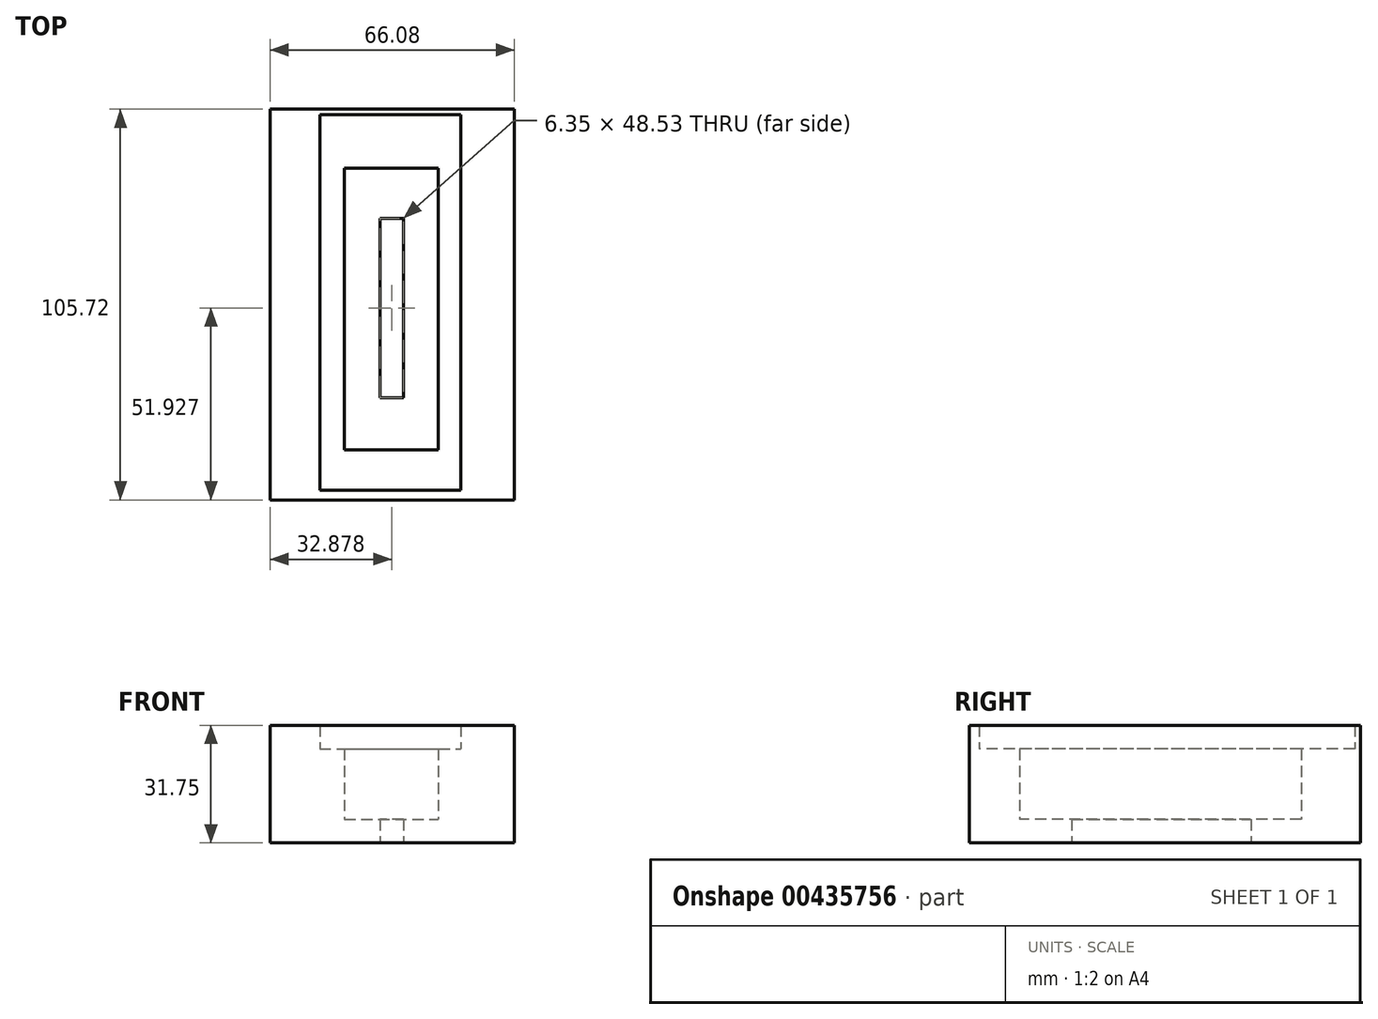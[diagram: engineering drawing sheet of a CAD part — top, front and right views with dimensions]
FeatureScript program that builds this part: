
annotation { "Feature Type Name" : "Feature", "Feature Type Description" : "" }
export const myFeature = defineFeature(function(context is Context, id is Id, definition is map)
    precondition{}
    {
        {
            var Q0;
            Q0=qCreatedBy(makeId("Top.planeOp"),FACE);
            var sketch = newSketch(context, id + "F0", { "sketchPlane" : qUnion([Q0])});
            skLineSegment(sketch, "E0.bottom", {"start": v(-32.9, 52.86) * mm, "end": v(33.19, 52.86) * mm});
            skLineSegment(sketch, "E0.top", {"start": v(-32.9, -52.86) * mm, "end": v(33.19, -52.86) * mm});
            skLineSegment(sketch, "E0.left", {"start": v(-32.9, 52.86) * mm, "end": v(-32.9, -52.86) * mm});
            skLineSegment(sketch, "E0.right", {"start": v(33.19, 52.86) * mm, "end": v(33.19, -52.86) * mm});
            skSolve(sketch);
        }
        {
            var Q0;
            Q0 = qSketchRegion(id + "F0", true);
            var Q1;
            Q1=makeQuery(id+"F0.imprint","IMPRINT",FACE,{"disambiguationData":[TD([[makeQuery(id+"F0.imprint","IMPRINT",EDGE,{"derivedFrom":sQuery(id+"F0.wireOp",EDGE,"E0.bottom")}),-1.0]])]});
            extrude(context, id + "F1", {"entities" : qUnion([Q0, Q1]), "depth" : 6.35 * mm});
        }
        {
            var Q0;
            Q0=makeQuery(id+"F1.opExtrude","CAP_FACE",FACE,{"disambiguationData":[OSD([sQuery(id+"F0.wireOp",EDGE,"E0.bottom"),sQuery(id+"F0.wireOp",EDGE,"E0.top"),sQuery(id+"F0.wireOp",EDGE,"E0.left"),sQuery(id+"F0.wireOp",EDGE,"E0.right")])],"isStart":false});
            var sketch = newSketch(context, id + "F2", { "sketchPlane" : qUnion([Q0])});
            skLineSegment(sketch, "E1.bottom", {"start": v(-19.5, 51.39) * mm, "end": v(18.6, 51.39) * mm});
            skLineSegment(sketch, "E1.top", {"start": v(-19.5, -50.21) * mm, "end": v(18.6, -50.21) * mm});
            skLineSegment(sketch, "E1.left", {"start": v(-19.5, 51.39) * mm, "end": v(-19.5, -50.21) * mm});
            skLineSegment(sketch, "E1.right", {"start": v(18.6, 51.39) * mm, "end": v(18.6, -50.21) * mm});
            skLineSegment(sketch, "E2.bottom", {"start": v(-10.32, 39.4) * mm, "end": v(10.5, 39.4) * mm});
            skLineSegment(sketch, "E2.top", {"start": v(-10.32, -41.4) * mm, "end": v(10.5, -41.4) * mm});
            skLineSegment(sketch, "E2.left", {"start": v(-10.32, 39.4) * mm, "end": v(-10.32, -41.4) * mm});
            skLineSegment(sketch, "E2.right", {"start": v(10.5, 39.4) * mm, "end": v(10.5, -41.4) * mm});
            skLineSegment(sketch, "E3.bottom", {"start": v(-3.62, 27.05) * mm, "end": v(3.44, 27.05) * mm});
            skLineSegment(sketch, "E3.top", {"start": v(-3.62, -32.57) * mm, "end": v(3.44, -32.57) * mm});
            skLineSegment(sketch, "E3.left", {"start": v(-3.62, 27.05) * mm, "end": v(-3.62, -32.57) * mm});
            skLineSegment(sketch, "E3.right", {"start": v(3.44, 27.05) * mm, "end": v(3.44, -32.57) * mm});
            skSolve(sketch);
        }
        {
            var Q0;
            Q0=makeQuery(id+"F2.imprint","IMPRINT",FACE,{"disambiguationData":[TD([[makeQuery(id+"F2.imprint","IMPRINT",EDGE,{"derivedFrom":sQuery(id+"F2.wireOp",EDGE,"E1.bottom")}),1.0]])]});
            extrude(context, id + "F3", {"entities" : qUnion([Q0]), "operationType" : NewBodyOperationType.ADD, "depth" : 25.4 * mm});
        }
        {
            var Q0;
            Q0=makeQuery(id+"F1.opExtrude","CAP_FACE",FACE,{"disambiguationData":[OSD([sQuery(id+"F0.wireOp",EDGE,"E0.bottom"),sQuery(id+"F0.wireOp",EDGE,"E0.top"),sQuery(id+"F0.wireOp",EDGE,"E0.left"),sQuery(id+"F0.wireOp",EDGE,"E0.right")])],"isStart":false});
            var sketch = newSketch(context, id + "F4", { "sketchPlane" : qUnion([Q0])});
            skLineSegment(sketch, "E4.bottom", {"start": v(-12.83, 36.9) * mm, "end": v(12.57, 36.9) * mm});
            skLineSegment(sketch, "E4.top", {"start": v(-12.83, -39.3) * mm, "end": v(12.57, -39.3) * mm});
            skLineSegment(sketch, "E4.left", {"start": v(-12.83, 36.9) * mm, "end": v(-12.83, -39.3) * mm});
            skLineSegment(sketch, "E4.right", {"start": v(12.57, 36.9) * mm, "end": v(12.57, -39.3) * mm});
            skSolve(sketch);
        }
        {
            var Q0;
            Q0=makeQuery(id+"F4.imprint","IMPRINT",FACE,{"disambiguationData":[TD([[makeQuery(id+"F4.imprint","IMPRINT",EDGE,{"derivedFrom":sQuery(id+"F4.wireOp",EDGE,"E4.bottom")}),1.0]])]});
            extrude(context, id + "F5", {"entities" : qUnion([Q0]), "operationType" : NewBodyOperationType.ADD, "depth" : 19.05 * mm});
        }
        {
            var Q0;
            Q0=makeQuery(id+"F1.opExtrude","CAP_FACE",FACE,{"disambiguationData":[OSD([sQuery(id+"F0.wireOp",EDGE,"E0.bottom"),sQuery(id+"F0.wireOp",EDGE,"E0.top"),sQuery(id+"F0.wireOp",EDGE,"E0.left"),sQuery(id+"F0.wireOp",EDGE,"E0.right")])],"isStart":false});
            var sketch = newSketch(context, id + "F6", { "sketchPlane" : qUnion([Q0])});
            skLineSegment(sketch, "E5.bottom", {"start": v(-3.19, 23.33) * mm, "end": v(3.16, 23.33) * mm});
            skLineSegment(sketch, "E5.top", {"start": v(-3.19, -25.2) * mm, "end": v(3.16, -25.2) * mm});
            skLineSegment(sketch, "E5.left", {"start": v(-3.19, 23.33) * mm, "end": v(-3.19, -25.2) * mm});
            skLineSegment(sketch, "E5.right", {"start": v(3.16, 23.33) * mm, "end": v(3.16, -25.2) * mm});
            skSolve(sketch);
        }
        {
            var Q0;
            Q0=makeQuery(id+"F6.imprint","IMPRINT",FACE,{"disambiguationData":[TD([[makeQuery(id+"F6.imprint","IMPRINT",EDGE,{"derivedFrom":sQuery(id+"F6.wireOp",EDGE,"E5.bottom")}),-1.0]])]});
            extrude(context, id + "F7", {"entities" : qUnion([Q0]), "operationType" : NewBodyOperationType.REMOVE, "depth" : 25.4 * mm, "hasSecondDirection" : true, "secondDirectionOppositeDirection" : true, "secondDirectionDepth" : 25.4 * mm});
        }
    });
